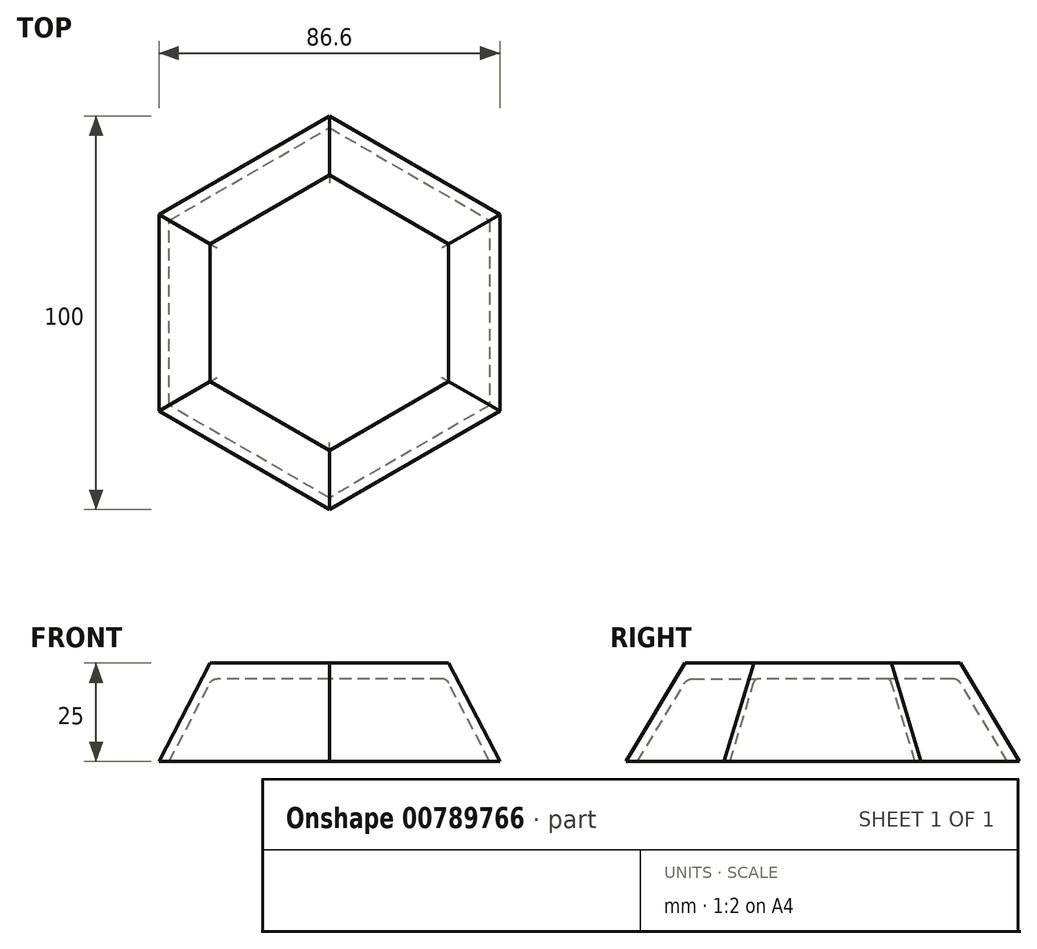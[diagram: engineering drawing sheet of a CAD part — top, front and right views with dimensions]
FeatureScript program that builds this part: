
annotation { "Feature Type Name" : "Feature", "Feature Type Description" : "" }
export const myFeature = defineFeature(function(context is Context, id is Id, definition is map)
    precondition{}
    {
        {
            var Q0;
            Q0=qCreatedBy(makeId("Top.planeOp"),FACE);
            var sketch = newSketch(context, id + "F0", { "sketchPlane" : qUnion([Q0])});
            skCircle(sketch, "E0.cCircle", {"center": v(0, 0) * mm, "radius": 35 * mm, "construction": true});
            skLineSegment(sketch, "E0.0", {"start": v(30.31, -17.5) * mm, "end": v(0, -35) * mm});
            skLineSegment(sketch, "E0.1", {"start": v(0, -35) * mm, "end": v(-30.31, -17.5) * mm});
            skLineSegment(sketch, "E0.2", {"start": v(-30.31, -17.5) * mm, "end": v(-30.31, 17.5) * mm});
            skLineSegment(sketch, "E0.3", {"start": v(-30.31, 17.5) * mm, "end": v(0, 35) * mm});
            skLineSegment(sketch, "E0.4", {"start": v(0, 35) * mm, "end": v(30.31, 17.5) * mm});
            skLineSegment(sketch, "E0.5", {"start": v(30.31, 17.5) * mm, "end": v(30.31, -17.5) * mm});
            skSolve(sketch);
        }
        {
            var Q0;
            Q0=qSketchRegion(id+"F0",true);
            extrude(context, id + "F1", {"entities" : qUnion([Q0]), "depth" : 25 * mm, "offsetDistance" : 25 * mm});
        }
        {
            var Q0;
            Q0=qCreatedBy(makeId("Top.planeOp"),FACE);
            var sketch = newSketch(context, id + "F2", { "sketchPlane" : qUnion([Q0])});
            skCircle(sketch, "E1.cCircle", {"center": v(0, 0) * mm, "radius": 50 * mm, "construction": true});
            skLineSegment(sketch, "E1.0", {"start": v(0, 50) * mm, "end": v(43.3, 25) * mm});
            skLineSegment(sketch, "E1.1", {"start": v(43.3, 25) * mm, "end": v(43.3, -25) * mm});
            skLineSegment(sketch, "E1.2", {"start": v(43.3, -25) * mm, "end": v(0, -50) * mm});
            skLineSegment(sketch, "E1.3", {"start": v(0, -50) * mm, "end": v(-43.3, -25) * mm});
            skLineSegment(sketch, "E1.4", {"start": v(-43.3, -25) * mm, "end": v(-43.3, 25) * mm});
            skLineSegment(sketch, "E1.5", {"start": v(-43.3, 25) * mm, "end": v(0, 50) * mm});
            skSolve(sketch);
        }
        {
            var Q1;
            Q1=makeQuery(id+"F1.opExtrude","CAP_FACE",FACE,{"disambiguationData":[OSD([sQuery(id+"F0.wireOp",EDGE,"E0.0"),sQuery(id+"F0.wireOp",EDGE,"E0.1"),sQuery(id+"F0.wireOp",EDGE,"E0.2"),sQuery(id+"F0.wireOp",EDGE,"E0.3"),sQuery(id+"F0.wireOp",EDGE,"E0.4"),sQuery(id+"F0.wireOp",EDGE,"E0.5")])],"isStart":false});
            var Q2;
            Q2=makeQuery(id+"F2.imprint","IMPRINT",FACE,{"disambiguationData":[TD([[makeQuery(id+"F2.imprint","IMPRINT",EDGE,{"derivedFrom":sQuery(id+"F2.wireOp",EDGE,"E1.0")}),-1.0]])]});
            loft(context, id + "F3", {"operationType" : NewBodyOperationType.ADD, "sheetProfilesArray" : [{ "sheetProfileEntities" : qUnion([Q1]) }, { "sheetProfileEntities" : qUnion([Q2]) }]});
        }
        {
            var Q0;
            Q0=qCreatedBy(makeId("Top.planeOp"),FACE);
            var sketch = newSketch(context, id + "F4", { "sketchPlane" : qUnion([Q0])});
            skCircle(sketch, "E2.cCircle", {"center": v(0, 0) * mm, "radius": 47 * mm, "construction": true});
            skLineSegment(sketch, "E2.0", {"start": v(0, -47) * mm, "end": v(-40.7, -23.5) * mm});
            skLineSegment(sketch, "E2.1", {"start": v(-40.7, -23.5) * mm, "end": v(-40.7, 23.5) * mm});
            skLineSegment(sketch, "E2.2", {"start": v(-40.7, 23.5) * mm, "end": v(0, 47) * mm});
            skLineSegment(sketch, "E2.3", {"start": v(0, 47) * mm, "end": v(40.7, 23.5) * mm});
            skLineSegment(sketch, "E2.4", {"start": v(40.7, 23.5) * mm, "end": v(40.7, -23.5) * mm});
            skLineSegment(sketch, "E2.5", {"start": v(40.7, -23.5) * mm, "end": v(0, -47) * mm});
            skSolve(sketch);
        }
        {
            var Q0;
            Q0=makeQuery(id+"F1.opExtrude","CAP_FACE",FACE,{"disambiguationData":[OSD([sQuery(id+"F0.wireOp",EDGE,"E0.0"),sQuery(id+"F0.wireOp",EDGE,"E0.1"),sQuery(id+"F0.wireOp",EDGE,"E0.2"),sQuery(id+"F0.wireOp",EDGE,"E0.3"),sQuery(id+"F0.wireOp",EDGE,"E0.4"),sQuery(id+"F0.wireOp",EDGE,"E0.5")])],"isStart":false});
            var sketch = newSketch(context, id + "F5", { "sketchPlane" : qUnion([Q0])});
            skCircle(sketch, "E3.cCircle", {"center": v(0, 0) * mm, "radius": 32 * mm, "construction": true});
            skLineSegment(sketch, "E3.0", {"start": v(0, 32) * mm, "end": v(27.71, 16) * mm});
            skLineSegment(sketch, "E3.1", {"start": v(27.71, 16) * mm, "end": v(27.71, -16) * mm});
            skLineSegment(sketch, "E3.2", {"start": v(27.71, -16) * mm, "end": v(0, -32) * mm});
            skLineSegment(sketch, "E3.3", {"start": v(0, -32) * mm, "end": v(-27.71, -16) * mm});
            skLineSegment(sketch, "E3.4", {"start": v(-27.71, -16) * mm, "end": v(-27.71, 16) * mm});
            skLineSegment(sketch, "E3.5", {"start": v(-27.71, 16) * mm, "end": v(0, 32) * mm});
            skSolve(sketch);
        }
        {
            var Q1;
            Q1=qSketchRegion(id+"F4",true);
            var Q2;
            Q2=qSketchRegion(id+"F5",true);
            loft(context, id + "F6", {"operationType" : NewBodyOperationType.REMOVE, "sheetProfilesArray" : [{ "sheetProfileEntities" : qUnion([Q1]) }, { "sheetProfileEntities" : qUnion([Q2]) }]});
        }
        {
            var Q0;
            Q0=makeQuery(id+"F1.opExtrude","CAP_FACE",FACE,{"disambiguationData":[OSD([sQuery(id+"F0.wireOp",EDGE,"E0.0"),sQuery(id+"F0.wireOp",EDGE,"E0.1"),sQuery(id+"F0.wireOp",EDGE,"E0.2"),sQuery(id+"F0.wireOp",EDGE,"E0.3"),sQuery(id+"F0.wireOp",EDGE,"E0.4"),sQuery(id+"F0.wireOp",EDGE,"E0.5")])],"isStart":false});
            var sketch = newSketch(context, id + "F7", { "sketchPlane" : qUnion([Q0])});
            skCircle(sketch, "E4.cCircle", {"center": v(0, 0) * mm, "radius": 35 * mm, "construction": true});
            skLineSegment(sketch, "E4.0", {"start": v(0, -35) * mm, "end": v(-30.31, -17.5) * mm});
            skLineSegment(sketch, "E4.1", {"start": v(-30.31, -17.5) * mm, "end": v(-30.31, 17.5) * mm});
            skLineSegment(sketch, "E4.2", {"start": v(-30.31, 17.5) * mm, "end": v(0, 35) * mm});
            skLineSegment(sketch, "E4.3", {"start": v(0, 35) * mm, "end": v(30.31, 17.5) * mm});
            skLineSegment(sketch, "E4.4", {"start": v(30.31, 17.5) * mm, "end": v(30.31, -17.5) * mm});
            skLineSegment(sketch, "E4.5", {"start": v(30.31, -17.5) * mm, "end": v(0, -35) * mm});
            skSolve(sketch);
        }
        {
            var Q0;
            Q0=qSketchRegion(id+"F7",true);
            extrude(context, id + "F8", {"entities" : qUnion([Q0]), "operationType" : NewBodyOperationType.ADD, "oppositeDirection" : true, "depth" : 4 * mm, "offsetDistance" : 25 * mm});
        }
        {
            var Q0;
            Q0=makeQuery(id+"F8.boolean.opBoolean","INTERSECT",EDGE,{"derivedFrom":[makeQuery(id+"F6.boolean.opBoolean","COPY",FACE,{"derivedFrom":makeQuery(id+"F6.opLoft","SWEPT_FACE",FACE,{"disambiguationData":[OSD([sQuery(id+"F4.wireOp",EDGE,"E2.0"),sQuery(id+"F4.wireOp",EDGE,"E2.1"),sQuery(id+"F4.wireOp",EDGE,"E2.5"),sQuery(id+"F5.wireOp",EDGE,"E3.2"),sQuery(id+"F5.wireOp",EDGE,"E3.3"),sQuery(id+"F5.wireOp",EDGE,"E3.4")])]})}),makeQuery(id+"F8.opExtrude","CAP_FACE",FACE,{"disambiguationData":[OSD([sQuery(id+"F7.wireOp",EDGE,"E4.0"),sQuery(id+"F7.wireOp",EDGE,"E4.1"),sQuery(id+"F7.wireOp",EDGE,"E4.2"),sQuery(id+"F7.wireOp",EDGE,"E4.3"),sQuery(id+"F7.wireOp",EDGE,"E4.4"),sQuery(id+"F7.wireOp",EDGE,"E4.5")])],"isStart":false})]});
            var Q1;
            Q1=makeQuery(id+"F8.boolean.opBoolean","INTERSECT",EDGE,{"derivedFrom":[makeQuery(id+"F6.boolean.opBoolean","COPY",FACE,{"derivedFrom":makeQuery(id+"F6.opLoft","SWEPT_FACE",FACE,{"disambiguationData":[OSD([sQuery(id+"F4.wireOp",EDGE,"E2.0"),sQuery(id+"F4.wireOp",EDGE,"E2.1"),sQuery(id+"F4.wireOp",EDGE,"E2.2"),sQuery(id+"F5.wireOp",EDGE,"E3.3"),sQuery(id+"F5.wireOp",EDGE,"E3.4"),sQuery(id+"F5.wireOp",EDGE,"E3.5")])]})}),makeQuery(id+"F8.opExtrude","CAP_FACE",FACE,{"disambiguationData":[OSD([sQuery(id+"F7.wireOp",EDGE,"E4.0"),sQuery(id+"F7.wireOp",EDGE,"E4.1"),sQuery(id+"F7.wireOp",EDGE,"E4.2"),sQuery(id+"F7.wireOp",EDGE,"E4.3"),sQuery(id+"F7.wireOp",EDGE,"E4.4"),sQuery(id+"F7.wireOp",EDGE,"E4.5")])],"isStart":false})]});
            var Q2;
            Q2=makeQuery(id+"F8.boolean.opBoolean","INTERSECT",EDGE,{"derivedFrom":[makeQuery(id+"F6.boolean.opBoolean","COPY",FACE,{"derivedFrom":makeQuery(id+"F6.opLoft","SWEPT_FACE",FACE,{"disambiguationData":[OSD([sQuery(id+"F4.wireOp",EDGE,"E2.0"),sQuery(id+"F4.wireOp",EDGE,"E2.4"),sQuery(id+"F4.wireOp",EDGE,"E2.5"),sQuery(id+"F5.wireOp",EDGE,"E3.1"),sQuery(id+"F5.wireOp",EDGE,"E3.2"),sQuery(id+"F5.wireOp",EDGE,"E3.3")])]})}),makeQuery(id+"F8.opExtrude","CAP_FACE",FACE,{"disambiguationData":[OSD([sQuery(id+"F7.wireOp",EDGE,"E4.0"),sQuery(id+"F7.wireOp",EDGE,"E4.1"),sQuery(id+"F7.wireOp",EDGE,"E4.2"),sQuery(id+"F7.wireOp",EDGE,"E4.3"),sQuery(id+"F7.wireOp",EDGE,"E4.4"),sQuery(id+"F7.wireOp",EDGE,"E4.5")])],"isStart":false})]});
            var Q3;
            Q3=makeQuery(id+"F8.boolean.opBoolean","INTERSECT",EDGE,{"derivedFrom":[makeQuery(id+"F6.boolean.opBoolean","COPY",FACE,{"derivedFrom":makeQuery(id+"F6.opLoft","SWEPT_FACE",FACE,{"disambiguationData":[OSD([sQuery(id+"F4.wireOp",EDGE,"E2.3"),sQuery(id+"F4.wireOp",EDGE,"E2.4"),sQuery(id+"F4.wireOp",EDGE,"E2.5"),sQuery(id+"F5.wireOp",EDGE,"E3.0"),sQuery(id+"F5.wireOp",EDGE,"E3.1"),sQuery(id+"F5.wireOp",EDGE,"E3.2")])]})}),makeQuery(id+"F8.opExtrude","CAP_FACE",FACE,{"disambiguationData":[OSD([sQuery(id+"F7.wireOp",EDGE,"E4.0"),sQuery(id+"F7.wireOp",EDGE,"E4.1"),sQuery(id+"F7.wireOp",EDGE,"E4.2"),sQuery(id+"F7.wireOp",EDGE,"E4.3"),sQuery(id+"F7.wireOp",EDGE,"E4.4"),sQuery(id+"F7.wireOp",EDGE,"E4.5")])],"isStart":false})]});
            var Q4;
            Q4=makeQuery(id+"F8.boolean.opBoolean","INTERSECT",EDGE,{"derivedFrom":[makeQuery(id+"F6.boolean.opBoolean","COPY",FACE,{"derivedFrom":makeQuery(id+"F6.opLoft","SWEPT_FACE",FACE,{"disambiguationData":[OSD([sQuery(id+"F4.wireOp",EDGE,"E2.2"),sQuery(id+"F4.wireOp",EDGE,"E2.3"),sQuery(id+"F4.wireOp",EDGE,"E2.4"),sQuery(id+"F5.wireOp",EDGE,"E3.0"),sQuery(id+"F5.wireOp",EDGE,"E3.1"),sQuery(id+"F5.wireOp",EDGE,"E3.5")])]})}),makeQuery(id+"F8.opExtrude","CAP_FACE",FACE,{"disambiguationData":[OSD([sQuery(id+"F7.wireOp",EDGE,"E4.0"),sQuery(id+"F7.wireOp",EDGE,"E4.1"),sQuery(id+"F7.wireOp",EDGE,"E4.2"),sQuery(id+"F7.wireOp",EDGE,"E4.3"),sQuery(id+"F7.wireOp",EDGE,"E4.4"),sQuery(id+"F7.wireOp",EDGE,"E4.5")])],"isStart":false})]});
            var Q5;
            Q5=makeQuery(id+"F8.boolean.opBoolean","INTERSECT",EDGE,{"derivedFrom":[makeQuery(id+"F6.boolean.opBoolean","COPY",FACE,{"derivedFrom":makeQuery(id+"F6.opLoft","SWEPT_FACE",FACE,{"disambiguationData":[OSD([sQuery(id+"F4.wireOp",EDGE,"E2.1"),sQuery(id+"F4.wireOp",EDGE,"E2.2"),sQuery(id+"F4.wireOp",EDGE,"E2.3"),sQuery(id+"F5.wireOp",EDGE,"E3.0"),sQuery(id+"F5.wireOp",EDGE,"E3.4"),sQuery(id+"F5.wireOp",EDGE,"E3.5")])]})}),makeQuery(id+"F8.opExtrude","CAP_FACE",FACE,{"disambiguationData":[OSD([sQuery(id+"F7.wireOp",EDGE,"E4.0"),sQuery(id+"F7.wireOp",EDGE,"E4.1"),sQuery(id+"F7.wireOp",EDGE,"E4.2"),sQuery(id+"F7.wireOp",EDGE,"E4.3"),sQuery(id+"F7.wireOp",EDGE,"E4.4"),sQuery(id+"F7.wireOp",EDGE,"E4.5")])],"isStart":false})]});
            fillet(context, id + "F9", {"entities" : qUnion([Q0, Q1, Q2, Q3, Q4, Q5]), "radius" : 2 * mm, "tangentPropagation" : true, "allowEdgeOverflow" : false});
        }
    });
